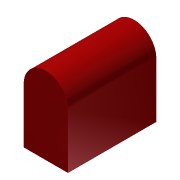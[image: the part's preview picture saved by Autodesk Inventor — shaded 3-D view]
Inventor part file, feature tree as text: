
AUTODESK INVENTOR PART (.ipt)
format: ipt  version: 2014 SP2 (Build 180247200, 247)  size: 82,944 bytes
history: native  units: mm
features: extrude x1, fillet x1, sketch x1
ambient origin geometry x8: Origin, YZ Plane, XZ Plane, XY Plane, X Axis, Y Axis, Z Axis, Center Point
bodies: Solid1 (feature_tree)
feature tree (3):
  extrude  "Extrusion1"  Depth=2.0mm
  fillet  "Fillet1"  Radius=1.0mm
  sketch  "Sketch2"  dims[d2=4.0mm d3=2.0mm d4=1.0mm d5=2.0mm d6=3.5mm d7=0.0mm d8=1.0mm]
